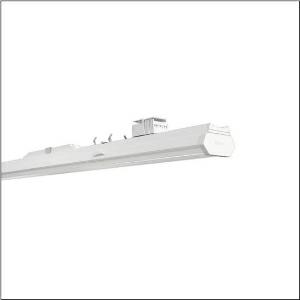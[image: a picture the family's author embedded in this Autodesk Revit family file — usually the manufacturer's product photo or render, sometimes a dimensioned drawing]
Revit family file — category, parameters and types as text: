
# Revit family: licross_r__11_protected_tw_51tp12tnt8xw_8db3
name_source: partatom
category: Lighting Fixtures
units: mm (PartAtom-declared; Revit-internal decimal feet)

## family parameters
Cut with Voids When Loaded = No
Host = Face
Light Source = No
Part Type = Normal
Room Calculation Point = No
Round Connector Dimension = Use Diameter
Shared = No

## types (1)
- --- (1 x LED 2700 K ... 6500 K, 8100 lm, 57.4 W, 2700K)
    Apparent Load = 57 VA
    CIE Flux Codes = 70 91 97 98 100
    Color Rendering = 80
    Color Temperature = 2700K
    Default Elevation = 1800 mm
    Description = Licross® 11 Protected TWluminaire insert, length: 1.500mm, width: 90mm, height: 101mm, LED rated luminous flux: 8.100lm, light colour: 8tw, control gear: DALI DT8, control gear: ECG DALI, with plug, 5-pole, with phase selection, mains connection: 220..240V, AC, 50/60Hz, halogen-free wiring, primary optical cover: cover, light emission: direct with ceiling illumination distribution, protection rating (complete): IP64, insulation class (complete): insulation class I (protective earthing), certification: CE, ENEC, VDE, protection symbol: D if used in an environment with conductive dust loads with corresponding accessories, permissible ambient temperature for indoor applications: -25..+40°C, reducing of maximum allowable ambient temperature of 5°C with ceiling mounting, corresponds to IFS (International Featured Standards) requirements for safety and quality in the food industry, packaging unit: 1 piece
    Height = 92 mm
    Lamp = 1 x LED 2700 K ... 6500 K
    Lamp Light Flux = 8100 lm
    Lamp Power = 57.4 W
    Lamp count = 1
    Length = 1500 mm
    Luminous efficacy = 141 lm/W
    Manufacturer = Siteco
    ModVariant = No
    Model = 51TP12TNT8XW
    Mounting Place = Ceiling
    Mounting Type = Pendant
    Number of Poles = 1
    OnlyDefault = Yes
    Power Factor = 1
    Product Name = Licross® 11 Protected TW
    Product group = luminaire insert
    ProductGroupID = 902
    Protection Class = Protection class I
    Protection Degree = IP 64
    RLX_Detail_Level = 1
    RlxData = <blob elided: 20393 chars, md5=ce7dcaa9>
    Socket = socket
    Standby Power = 0 W
    System Light Flux = 8100 lm
    System Power = 57 W
    Type Comments = individual setting: CCT=2700K
    Type Image = l_1256148.jpg
    URL = http://relux.com
    VarID = @adj_137927
    Voltage = 0 V
    Weight = 0.00 kg
    Width = 88 mm

## geometry (parser evidence)
native form markers: Blend x4, Sweep x10
no freeform markers — native parametric forms only
